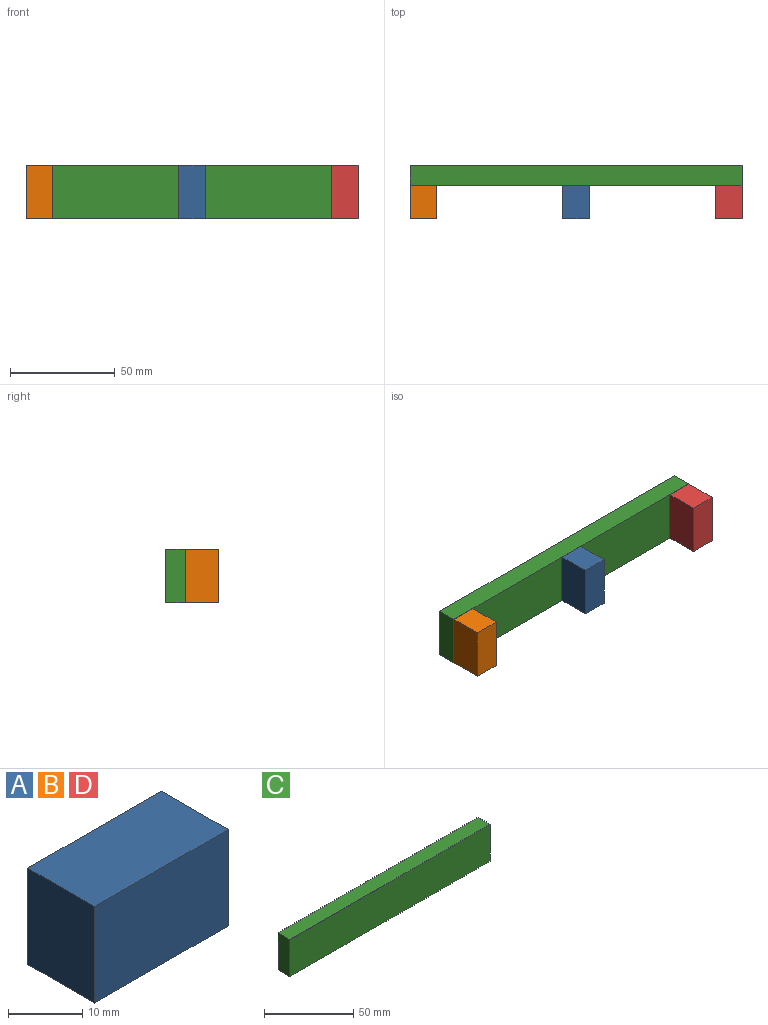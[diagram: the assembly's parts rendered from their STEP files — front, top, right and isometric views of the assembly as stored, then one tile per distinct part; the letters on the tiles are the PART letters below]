
ASSEMBLY  parts=4 mates=3
PART A: 6 faces, bbox 25.4x12.7x15.9 mm
  f0: plane 15.88x12.7mm, normal (-1,0,0), area 201.6mm2, adj f1,f3,f4,f5
  f1: plane 25.4x12.7mm, normal (0,0,-1), area 322.6mm2, adj f0,f2,f4,f5
  f2: plane 15.88x12.7mm, normal (1,0,0), area 201.6mm2, adj f1,f3,f4,f5
  f3: plane 25.4x12.7mm, normal (0,0,1), area 322.6mm2, adj f0,f2,f4,f5
  f4: plane 25.4x15.88mm, normal (0,-1,0), area 403.2mm2, adj f0,f1,f2,f3
  f5: plane 25.4x15.88mm, normal (0,1,0), area 403.2mm2, adj f0,f1,f2,f3
PART B: same geometry as A
PART C: 6 faces, bbox 158.8x9.5x25.4 mm
  f0: plane 25.4x9.53mm, normal (-1,0,0), area 241.9mm2, adj f1,f3,f4,f5
  f1: plane 158.75x9.53mm, normal (0,0,-1), area 1512.1mm2, adj f0,f2,f4,f5
  f2: plane 25.4x9.53mm, normal (1,0,0), area 241.9mm2, adj f1,f3,f4,f5
  f3: plane 158.75x9.53mm, normal (0,0,1), area 1512.1mm2, adj f0,f2,f4,f5
  f4: plane 158.75x25.4mm, normal (0,-1,0), area 4032.3mm2, adj f0,f1,f2,f3
  f5: plane 158.75x25.4mm, normal (0,1,0), area 4032.3mm2, adj f0,f1,f2,f3
PART D: same geometry as A
PLACE A rot(axis=(0.58,0.58,-0.58),120deg) t=(-2.38,-23.38,99.63)mm
PLACE B rot(axis=(-0.58,-0.58,-0.58),120deg) t=(-75.4,-105.38,74.23)mm
PLACE C rot(axis=(0,0,1),180deg) t=(70.65,-56.44,99.63)mm fixed
PLACE D rot(axis=(-0.58,-0.58,-0.58),120deg) t=(70.65,-105.38,74.23)mm
MATE planar C.f5 <-> D.f3  axis (0,-1,0) through (70.65,-56.44,86.93)mm
MATE planar B.f3 <-> C.f5  axis (0,1,0) through (-88.1,-56.44,86.93)mm
MATE planar A.f1 <-> C.f5  axis (0,1,0) through (-8.73,-56.44,86.93)mm
